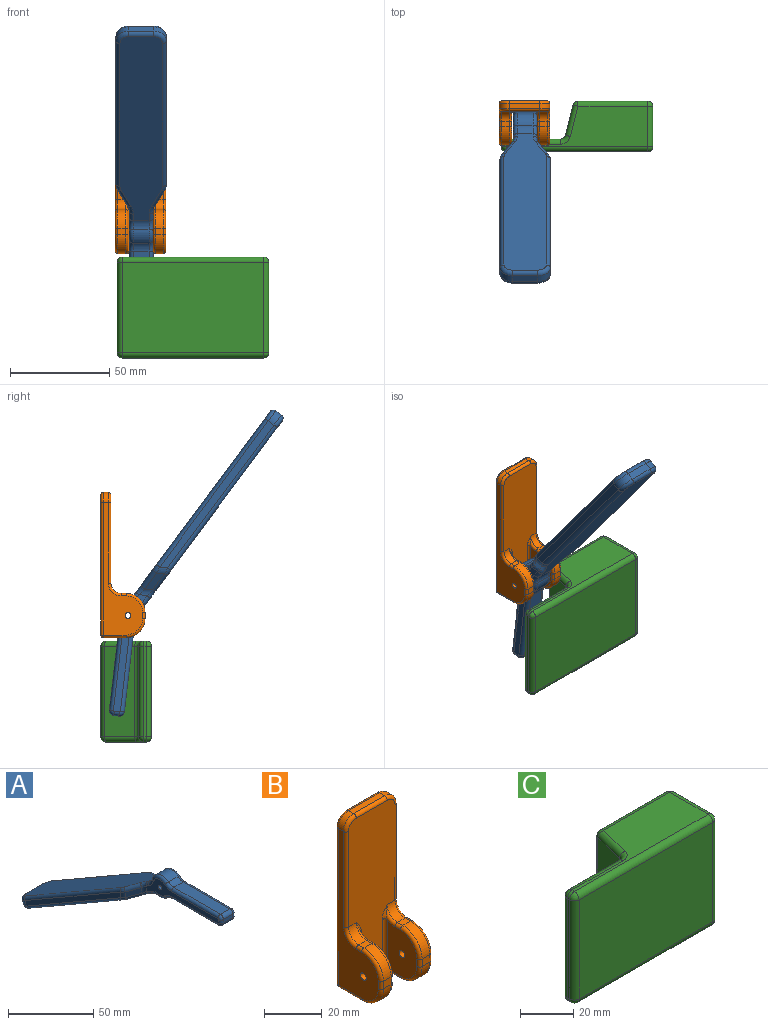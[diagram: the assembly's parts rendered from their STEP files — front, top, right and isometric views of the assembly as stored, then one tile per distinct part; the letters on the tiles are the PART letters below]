
ASSEMBLY  parts=3 mates=2
PART A: 75 faces, bbox 26.4x162.3x74.5 mm
  f0: plane 7.87x2.54mm, normal (0,-1,0), area 20mm2, adj f25,f26,f27,f74
  f1: plane 38.67x7.87mm, normal (0,0,-1), area 304.5mm2, adj f19,f26,f30,f70
  f2: cylinder r=7.62mm len=7.87mm, axis (-1,0,0), area 59.4mm2, adj f19,f20,f34,f66
  f3: plane 99.92x57.69mm, normal (0,-0.5,-0.87), area 2273.2mm2, adj f20,f38,f40,f42,f44,f46,f48,f50
  f4: plane 99.92x57.69mm, normal (0,0.5,0.87), area 2300.9mm2, adj f21,f39,f41,f43,f45,f47,f49,f51
  f5: cylinder r=7.62mm len=12.53mm, axis (-1,0,0), area 122.2mm2, adj f21,f22,f35,f67
  f6: plane 38.67x7.87mm, normal (0,0,1), area 304.5mm2, adj f22,f25,f31,f71
  f7: plane 12.7x3.08mm, normal (0,0.87,-0.5), area 45.2mm2, adj f23,f24,f50,f51
  f8: plane 79.32x48.87mm, normal (1,0,0), area 322mm2, adj f16,f24,f46,f47
  f9: plane 79.32x48.87mm, normal (-1,0,0), area 322mm2, adj f18,f23,f54,f55
  f10: plane 59.77x13.99mm, normal (1,0,0), area 279.9mm2, adj f14,f15,f27,f28,f29,f30,f31,f32
  f11: plane 9.14x8.71mm, normal (0.87,-0.5,0), area 41.3mm2, adj f15,f16,f42,f43
  f12: plane 59.77x13.99mm, normal (-1,0,0), area 279.9mm2, adj f14,f17,f62,f63,f64,f65,f66,f67
  f13: plane 9.14x8.71mm, normal (-0.87,-0.5,0), area 41.3mm2, adj f17,f18,f58,f59
  f14: cylinder r=1.4mm len=11.94mm, axis (-1,0,0), area 104.8mm2, adj f10,f12
  f15: cylinder r=6.35mm len=6.53mm, axis (0,0,1), area 13.7mm2, adj f10,f11,f40,f41
  f16: cylinder r=6.35mm len=5.35mm, axis (0,0,1), area 13.7mm2, adj f8,f11,f44,f45
  f17: cylinder r=6.35mm len=6.53mm, axis (0,0,1), area 13.7mm2, adj f12,f13,f60,f61
  f18: cylinder r=6.35mm len=5.35mm, axis (0,0,1), area 13.7mm2, adj f9,f13,f56,f57
  f19: cylinder r=6.35mm len=7.87mm, axis (-1,0,0), area 37.8mm2, adj f1,f2,f32,f68
  f20: cylinder r=6.35mm len=7.87mm, axis (-1,0,0), area 37.8mm2, adj f2,f3,f36,f64
  f21: cylinder r=6.35mm len=7.87mm, axis (-1,0,0), area 37.8mm2, adj f4,f5,f37,f65
  f22: cylinder r=6.35mm len=7.87mm, axis (-1,0,0), area 37.8mm2, adj f5,f6,f33,f69
  f23: cylinder r=6.35mm len=7.28mm, axis (0,0.5,0.87), area 35.5mm2, adj f7,f9,f52,f53
  f24: cylinder r=6.35mm len=7.28mm, axis (0,-0.5,-0.87), area 35.5mm2, adj f7,f8,f48,f49
  f25: cylinder r=2.54mm len=7.87mm, axis (1,0,0), area 31.4mm2, adj f0,f6,f29,f73
  f26: cylinder r=2.54mm len=7.87mm, axis (-1,0,0), area 31.4mm2, adj f0,f1,f28,f72
  f27: cylinder r=2.03mm len=2.54mm, axis (0,0,-1), area 8.1mm2, adj f0,f10,f28,f29
  f28: torus R=0.51mm, axis (-1,0,0), area 9mm2, adj f10,f26,f27,f30
  f29: torus R=0.51mm, axis (-1,0,0), area 9mm2, adj f10,f25,f27,f31
  f30: cylinder r=2.03mm len=38.67mm, axis (0,-1,0), area 123.4mm2, adj f1,f10,f28,f32
  f31: cylinder r=2.03mm len=38.67mm, axis (0,1,0), area 123.4mm2, adj f6,f10,f29,f33
  f32: torus R=8.38mm, axis (-1,0,0), area 17.1mm2, adj f10,f19,f30,f34
  f33: torus R=8.38mm, axis (-1,0,0), area 17.1mm2, adj f10,f22,f31,f35
  f34: torus R=5.59mm, axis (-1,0,0), area 21.7mm2, adj f2,f10,f32,f36
  f35: torus R=5.59mm, axis (-1,0,0), area 44.7mm2, adj f5,f10,f33,f37
  f36: torus R=8.38mm, axis (-1,0,0), area 17.1mm2, adj f10,f20,f34,f38
  f37: torus R=8.38mm, axis (-1,0,0), area 17.1mm2, adj f10,f21,f35,f39
  f38: cylinder r=2.03mm len=4.6mm, axis (0,-0.87,0.5), area 13.2mm2, adj f3,f10,f36,f40
  f39: cylinder r=2.03mm len=2.82mm, axis (0,0.87,-0.5), area 6.7mm2, adj f4,f10,f37,f41
  f40: bspline ~5.76x5.08mm, area 13mm2, adj f3,f15,f38,f42
  f41: bspline ~7.51x5.71mm, area 15.1mm2, adj f4,f15,f39,f43
  f42: cylinder r=2.03mm len=8.98mm, axis (-0.45,-0.77,0.45), area 30.1mm2, adj f3,f11,f40,f44
  f43: cylinder r=2.03mm len=10.74mm, axis (0.45,0.77,-0.45), area 41.7mm2, adj f4,f11,f41,f45
  f44: bspline ~3.43x3.01mm, area 9.2mm2, adj f3,f16,f42,f46
  f45: bspline ~6.1x4.62mm, area 11.1mm2, adj f4,f16,f43,f47
  f46: cylinder r=2.03mm len=78.55mm, axis (0,-0.87,0.5), area 285.8mm2, adj f3,f8,f44,f48
  f47: cylinder r=2.03mm len=80.33mm, axis (0,0.87,-0.5), area 292.3mm2, adj f4,f8,f45,f49
  f48: torus R=4.32mm, axis (0,0.5,0.87), area 28.1mm2, adj f3,f24,f46,f50
  f49: torus R=4.32mm, axis (0,-0.5,-0.87), area 28.1mm2, adj f4,f24,f47,f51
  f50: cylinder r=2.03mm len=12.7mm, axis (-1,0,0), area 40.5mm2, adj f3,f7,f48,f52
  f51: cylinder r=2.03mm len=12.7mm, axis (-1,0,0), area 40.5mm2, adj f4,f7,f49,f53
  f52: torus R=4.32mm, axis (0,0.5,0.87), area 28.1mm2, adj f3,f23,f50,f54
  f53: torus R=4.32mm, axis (0,-0.5,-0.87), area 28.1mm2, adj f4,f23,f51,f55
  f54: cylinder r=2.03mm len=78.55mm, axis (0,0.87,-0.5), area 285.8mm2, adj f3,f9,f52,f56
  f55: cylinder r=2.03mm len=80.33mm, axis (0,-0.87,0.5), area 292.3mm2, adj f4,f9,f53,f57
  f56: bspline ~3.43x3.01mm, area 9.2mm2, adj f3,f18,f54,f58
  f57: bspline ~5.36x4.29mm, area 11.1mm2, adj f4,f18,f55,f59
  f58: cylinder r=2.03mm len=8.98mm, axis (-0.45,0.77,-0.45), area 30.1mm2, adj f3,f13,f56,f60
  f59: cylinder r=2.03mm len=10.74mm, axis (0.45,-0.77,0.45), area 41.7mm2, adj f4,f13,f57,f61
  f60: bspline ~6.85x5.71mm, area 13mm2, adj f3,f17,f58,f62
  f61: bspline ~7.51x5.71mm, area 15.1mm2, adj f4,f17,f59,f63
  f62: cylinder r=2.03mm len=4.6mm, axis (0,0.87,-0.5), area 13.2mm2, adj f3,f12,f60,f64
  f63: cylinder r=2.03mm len=2.82mm, axis (0,-0.87,0.5), area 6.7mm2, adj f4,f12,f61,f65
  f64: torus R=8.38mm, axis (-1,0,0), area 17.1mm2, adj f12,f20,f62,f66
  f65: torus R=8.38mm, axis (-1,0,0), area 17.1mm2, adj f12,f21,f63,f67
  f66: torus R=5.59mm, axis (-1,0,0), area 21.7mm2, adj f2,f12,f64,f68
  f67: torus R=5.59mm, axis (-1,0,0), area 44.7mm2, adj f5,f12,f65,f69
  f68: torus R=8.38mm, axis (-1,0,0), area 17.1mm2, adj f12,f19,f66,f70
  f69: torus R=8.38mm, axis (-1,0,0), area 17.1mm2, adj f12,f22,f67,f71
  f70: cylinder r=2.03mm len=38.67mm, axis (0,1,0), area 123.4mm2, adj f1,f12,f68,f72
  f71: cylinder r=2.03mm len=38.67mm, axis (0,-1,0), area 123.4mm2, adj f6,f12,f69,f73
  f72: torus R=0.51mm, axis (-1,0,0), area 9mm2, adj f12,f26,f70,f74
  f73: torus R=0.51mm, axis (-1,0,0), area 9mm2, adj f12,f25,f71,f74
  f74: cylinder r=2.03mm len=2.54mm, axis (0,0,1), area 8.1mm2, adj f0,f12,f72,f73
PART B: 66 faces, bbox 26.2x23x74.2 mm
  f0: plane 3.81x2.54mm, normal (0,0,1), area 9.7mm2, adj f16,f19,f45,f63
  f1: plane 3.81x2.54mm, normal (0,0,1), area 9.7mm2, adj f17,f18,f31,f48
  f2: plane 70.49x22.86mm, normal (0,1,0), area 1605.1mm2, adj f22,f25,f26,f29,f32,f33
  f3: plane 66.68x19.69mm, normal (-1,0,0), area 480.1mm2, adj f13,f21,f23,f24,f26,f27,f28,f31
  f4: plane 3.81x3.18mm, normal (0,-1,0), area 12.1mm2, adj f15,f17,f24,f49
  f5: plane 20.96x14.61mm, normal (1,0,0), area 253.7mm2, adj f13,f47,f48,f49,f50,f51,f53,f54
  f6: plane 70.49x22.86mm, normal (0,-1,0), area 1283.6mm2, adj f18,f19,f36,f38,f40,f42,f44,f52
  f7: plane 20.96x14.61mm, normal (-1,0,0), area 253.7mm2, adj f12,f56,f57,f59,f61,f62,f63,f65
  f8: plane 3.81x3.18mm, normal (0,-1,0), area 12.1mm2, adj f14,f16,f41,f59
  f9: plane 66.68x19.69mm, normal (1,0,0), area 480.1mm2, adj f12,f20,f32,f37,f39,f41,f43,f44
  f10: plane 22.86x11.43mm, normal (0,0,-1), area 128.6mm2, adj f14,f15,f27,f33,f37,f53,f55,f57
  f11: plane 15.24x2.54mm, normal (0,0,1), area 38.7mm2, adj f20,f21,f25,f40
  f12: cylinder r=1.4mm len=6.35mm, axis (1,0,0), area 55.7mm2, adj f7,f9
  f13: cylinder r=1.4mm len=6.35mm, axis (1,0,0), area 55.7mm2, adj f3,f5
  f14: cylinder r=9.53mm len=9.53mm, axis (1,0,0), area 57mm2, adj f8,f10,f39,f56
  f15: cylinder r=9.53mm len=9.53mm, axis (1,0,0), area 57mm2, adj f4,f10,f23,f51
  f16: cylinder r=9.53mm len=9.53mm, axis (-1,0,0), area 57mm2, adj f0,f8,f43,f61
  f17: cylinder r=9.53mm len=9.53mm, axis (-1,0,0), area 57mm2, adj f1,f4,f28,f47
  f18: cylinder r=5.08mm len=5.08mm, axis (1,0,0), area 30.4mm2, adj f1,f6,f34,f50
  f19: cylinder r=5.08mm len=5.08mm, axis (1,0,0), area 30.4mm2, adj f0,f6,f46,f65
  f20: cylinder r=5.08mm len=5.08mm, axis (0,-1,0), area 20.3mm2, adj f9,f11,f29,f42
  f21: cylinder r=5.08mm len=5.08mm, axis (0,1,0), area 20.3mm2, adj f3,f11,f22,f38
  f22: torus R=3.81mm, axis (0,1,0), area 14.5mm2, adj f2,f21,f25,f26
  f23: torus R=8.26mm, axis (-1,0,0), area 28.4mm2, adj f3,f15,f24,f27
  f24: cylinder r=1.27mm len=3.18mm, axis (0,0,-1), area 6.3mm2, adj f3,f4,f23,f28
  f25: cylinder r=1.27mm len=15.24mm, axis (1,0,0), area 30.4mm2, adj f2,f11,f22,f29
  f26: cylinder r=1.27mm len=66.68mm, axis (0,0,-1), area 133mm2, adj f2,f3,f22,f30
  f27: cylinder r=1.27mm len=11.43mm, axis (0,-1,0), area 22.8mm2, adj f3,f10,f23,f30
  f28: torus R=8.26mm, axis (-1,0,0), area 28.4mm2, adj f3,f17,f24,f31
  f29: torus R=3.81mm, axis (0,1,0), area 14.5mm2, adj f2,f20,f25,f32
  f30: sphere r=1.27mm, area 2.5mm2, adj f26,f27,f33
  f31: cylinder r=1.27mm len=2.54mm, axis (0,1,0), area 5.1mm2, adj f1,f3,f28,f34
  f32: cylinder r=1.27mm len=66.68mm, axis (0,0,-1), area 133mm2, adj f2,f9,f29,f35
  f33: cylinder r=1.27mm len=22.86mm, axis (-1,0,0), area 45.6mm2, adj f2,f10,f30,f35
  f34: torus R=6.35mm, axis (-1,0,0), area 17.4mm2, adj f3,f18,f31,f36
  f35: sphere r=1.27mm, area 2.5mm2, adj f32,f33,f37
  f36: cylinder r=1.27mm len=40.64mm, axis (0,0,-1), area 81.1mm2, adj f3,f6,f34,f38
  f37: cylinder r=1.27mm len=11.43mm, axis (0,1,0), area 22.8mm2, adj f9,f10,f35,f39
  f38: torus R=3.81mm, axis (0,-1,0), area 14.5mm2, adj f6,f21,f36,f40
  f39: torus R=8.26mm, axis (1,0,0), area 28.4mm2, adj f9,f14,f37,f41
  f40: cylinder r=1.27mm len=15.24mm, axis (-1,0,0), area 30.4mm2, adj f6,f11,f38,f42
  f41: cylinder r=1.27mm len=3.18mm, axis (0,0,-1), area 6.3mm2, adj f8,f9,f39,f43
  f42: torus R=3.81mm, axis (0,-1,0), area 14.5mm2, adj f6,f20,f40,f44
  f43: torus R=8.26mm, axis (1,0,0), area 28.4mm2, adj f9,f16,f41,f45
  f44: cylinder r=1.27mm len=40.64mm, axis (0,0,-1), area 81.1mm2, adj f6,f9,f42,f46
  f45: cylinder r=1.27mm len=2.54mm, axis (0,-1,0), area 5.1mm2, adj f0,f9,f43,f46
  f46: torus R=6.35mm, axis (1,0,0), area 17.4mm2, adj f9,f19,f44,f45
  f47: torus R=8.26mm, axis (1,0,0), area 28.4mm2, adj f5,f17,f48,f49
  f48: cylinder r=1.27mm len=2.54mm, axis (0,-1,0), area 5.1mm2, adj f1,f5,f47,f50
  f49: cylinder r=1.27mm len=3.18mm, axis (0,0,-1), area 6.3mm2, adj f4,f5,f47,f51
  f50: torus R=6.35mm, axis (1,0,0), area 11.2mm2, adj f5,f18,f48,f52
  f51: torus R=8.26mm, axis (1,0,0), area 28.4mm2, adj f5,f15,f49,f53
  f52: bspline ~5.94x2.54mm, area 5.6mm2, adj f6,f50,f54
  f53: cylinder r=1.27mm len=6.35mm, axis (0,1,0), area 12.7mm2, adj f5,f10,f51,f55
  f54: cylinder r=1.27mm len=20.96mm, axis (0,0,1), area 41.8mm2, adj f5,f6,f52,f55
  f55: torus R=2.54mm, axis (0,0,1), area 5.4mm2, adj f10,f53,f54,f58
  f56: torus R=8.26mm, axis (-1,0,0), area 28.4mm2, adj f7,f14,f57,f59
  f57: cylinder r=1.27mm len=6.35mm, axis (0,-1,0), area 12.7mm2, adj f7,f10,f56,f60
  f58: cylinder r=1.27mm len=10.16mm, axis (1,0,0), area 20.3mm2, adj f6,f10,f55,f60
  f59: cylinder r=1.27mm len=3.18mm, axis (0,0,-1), area 6.3mm2, adj f7,f8,f56,f61
  f60: torus R=2.54mm, axis (0,0,1), area 5.4mm2, adj f10,f57,f58,f62
  f61: torus R=8.26mm, axis (-1,0,0), area 28.4mm2, adj f7,f16,f59,f63
  f62: cylinder r=1.27mm len=20.96mm, axis (0,0,1), area 41.8mm2, adj f6,f7,f60,f64
  f63: cylinder r=1.27mm len=2.54mm, axis (0,1,0), area 5.1mm2, adj f0,f7,f61,f65
  f64: bspline ~5.94x2.54mm, area 5.6mm2, adj f6,f62,f65
  f65: torus R=6.35mm, axis (-1,0,0), area 11.2mm2, adj f7,f19,f63,f64
PART C: 38 faces, bbox 76.2x25.4x50.8 mm
  f0: plane 71.12x20.32mm, normal (0,0,-1), area 808.6mm2, adj f8,f11,f15,f20,f25,f26,f30
  f1: plane 45.72x20.32mm, normal (1,0,0), area 929mm2, adj f11,f12,f21,f22
  f2: plane 71.12x20.32mm, normal (0,0,1), area 808.6mm2, adj f13,f22,f23,f32,f33,f36,f37
  f3: plane 45.72x1.27mm, normal (-1,0,0), area 58.1mm2, adj f14,f15,f23,f24
  f4: plane 71.12x45.72mm, normal (0,-1,0), area 3251.6mm2, adj f8,f12,f13,f14
  f5: plane 45.72x27.23mm, normal (0,1,0), area 1244.8mm2, adj f24,f25,f33,f34
  f6: plane 45.72x35.16mm, normal (0,1,0), area 1607.7mm2, adj f20,f21,f31,f32
  f7: plane 45.72x15.2mm, normal (-0.97,0.24,0), area 716.4mm2, adj f26,f31,f34,f37
  f8: cylinder r=2.54mm len=71.12mm, axis (-1,0,0), area 283.8mm2, adj f0,f4,f9,f10
  f9: sphere r=2.54mm, area 10.1mm2, adj f8,f11,f12
  f10: sphere r=2.54mm, area 10.1mm2, adj f8,f14,f15
  f11: cylinder r=2.54mm len=20.32mm, axis (0,-1,0), area 81.1mm2, adj f0,f1,f9,f16
  f12: cylinder r=2.54mm len=45.72mm, axis (0,0,-1), area 182.4mm2, adj f1,f4,f9,f17
  f13: cylinder r=2.54mm len=71.12mm, axis (1,0,0), area 283.8mm2, adj f2,f4,f17,f18
  f14: cylinder r=2.54mm len=45.72mm, axis (0,0,1), area 182.4mm2, adj f3,f4,f10,f18
  f15: cylinder r=2.54mm len=2.54mm, axis (0,1,0), area 5.1mm2, adj f0,f3,f10,f19
  f16: sphere r=2.54mm, area 10.1mm2, adj f11,f20,f21
  f17: sphere r=2.54mm, area 10.1mm2, adj f12,f13,f22
  f18: sphere r=2.54mm, area 10.1mm2, adj f13,f14,f23
  f19: sphere r=2.54mm, area 10.1mm2, adj f15,f24,f25
  f20: cylinder r=2.54mm len=35.16mm, axis (-1,0,0), area 140.3mm2, adj f0,f6,f16,f27
  f21: cylinder r=2.54mm len=45.72mm, axis (0,0,-1), area 182.4mm2, adj f1,f6,f16,f28
  f22: cylinder r=2.54mm len=20.32mm, axis (0,1,0), area 81.1mm2, adj f1,f2,f17,f28
  f23: cylinder r=2.54mm len=2.54mm, axis (0,-1,0), area 5.1mm2, adj f2,f3,f18,f29
  f24: cylinder r=2.54mm len=45.72mm, axis (0,0,-1), area 182.4mm2, adj f3,f5,f19,f29
  f25: cylinder r=2.54mm len=27.23mm, axis (1,0,0), area 108.6mm2, adj f0,f5,f19,f30
  f26: cylinder r=2.54mm len=15.82mm, axis (-0.24,-0.97,0), area 62.5mm2, adj f0,f7,f27,f30
  f27: sphere r=2.54mm, area 8.6mm2, adj f20,f26,f31
  f28: sphere r=2.54mm, area 10.1mm2, adj f21,f22,f32
  f29: sphere r=2.54mm, area 10.1mm2, adj f23,f24,f33
  f30: torus R=5.08mm, axis (0,0,-1), area 18.3mm2, adj f0,f25,f26,f34
  f31: cylinder r=2.54mm len=45.72mm, axis (0,0,-1), area 154mm2, adj f6,f7,f27,f35
  f32: cylinder r=2.54mm len=35.16mm, axis (1,0,0), area 140.3mm2, adj f2,f6,f28,f35
  f33: cylinder r=2.54mm len=27.23mm, axis (-1,0,0), area 108.6mm2, adj f2,f5,f29,f36
  f34: cylinder r=2.54mm len=45.72mm, axis (0,0,1), area 154mm2, adj f5,f7,f30,f36
  f35: sphere r=2.54mm, area 8.6mm2, adj f31,f32,f37
  f36: torus R=5.08mm, axis (0,0,-1), area 18.3mm2, adj f2,f33,f34,f37
  f37: cylinder r=2.54mm len=15.82mm, axis (-0.24,-0.97,0), area 62.5mm2, adj f2,f7,f35,f36
PLACE A rot(axis=(0,0.66,0.75),180deg) t=(13.08,-13.65,-25.27)mm
PLACE B t=(0,0,-36.38)mm
PLACE C t=(64.57,-19.05,-88.9)mm
MATE revolute A.f67 <-> B.f12  axis (1,0,0) through (6.35,-13.65,-25.27)mm
MATE fastened C.f6 <-> B.f2  axis (0,1,0) through (44.45,0,-63.5)mm
